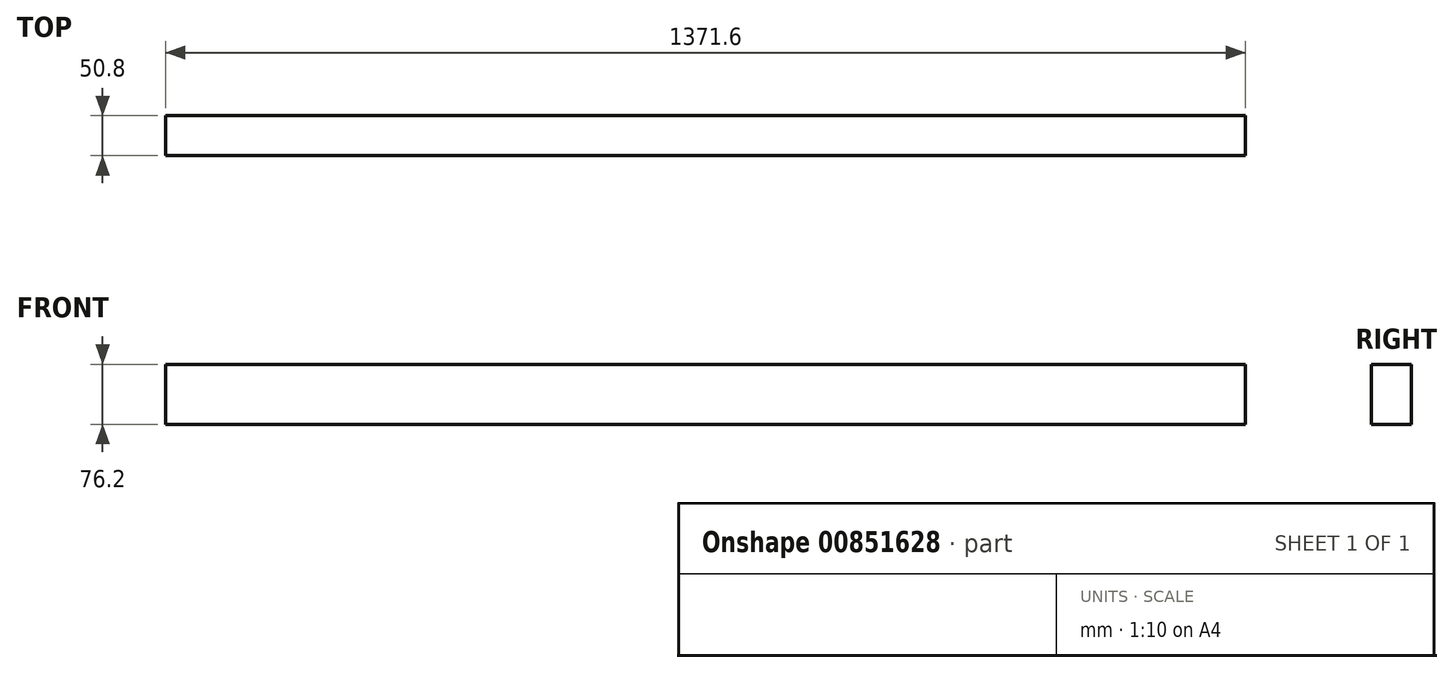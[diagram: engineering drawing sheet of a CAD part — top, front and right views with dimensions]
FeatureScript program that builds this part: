
annotation { "Feature Type Name" : "Feature", "Feature Type Description" : "" }
export const myFeature = defineFeature(function(context is Context, id is Id, definition is map)
    precondition{}
    {
        {
            var Q0;
            Q0=qCreatedBy(makeId("Front.planeOp"),FACE);
            var sketch = newSketch(context, id + "F0", { "sketchPlane" : qUnion([Q0])});
            skLineSegment(sketch, "E0", {"start": v(-803.07, 43.36) * mm, "end": v(568.53, 43.36) * mm});
            skLineSegment(sketch, "E1", {"start": v(-803.07, 43.36) * mm, "end": v(-803.07, -32.84) * mm});
            skLineSegment(sketch, "E2", {"start": v(568.53, 43.36) * mm, "end": v(568.53, -32.84) * mm});
            skLineSegment(sketch, "E3", {"start": v(568.53, -32.84) * mm, "end": v(-803.07, -32.84) * mm});
            skSolve(sketch);
        }
        {
            var Q0;
            Q0=qSketchRegion(id+"F0",true);
            extrude(context, id + "F1", {"entities" : qUnion([Q0]), "depth" : 50.8 * mm, "offsetDistance" : 25.4 * mm});
        }
    });
